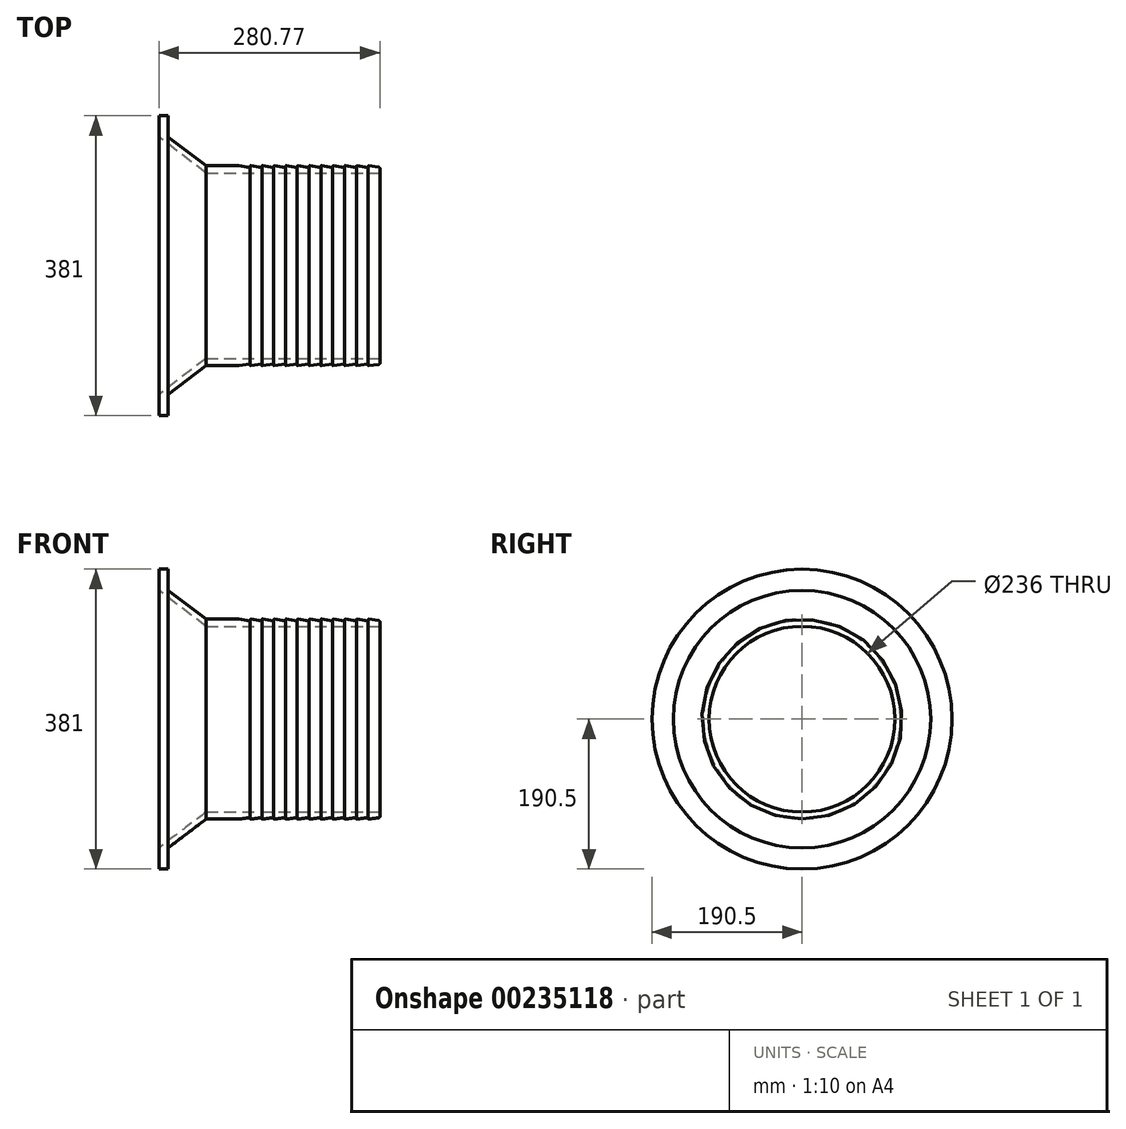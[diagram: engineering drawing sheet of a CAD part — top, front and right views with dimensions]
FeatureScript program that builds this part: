
annotation { "Feature Type Name" : "Feature", "Feature Type Description" : "" }
export const myFeature = defineFeature(function(context is Context, id is Id, definition is map)
    precondition{}
    {
        {
            var Q0;
            Q0=qCreatedBy(makeId("Front.planeOp"),FACE);
            var sketch = newSketch(context, id + "F0", { "sketchPlane" : qUnion([Q0])});
            skLineSegment(sketch, "E0", {"start": v(-1.73, 125.24) * mm, "end": v(-14.43, 127) * mm});
            skLineSegment(sketch, "E1", {"start": v(-15, 126.5) * mm, "end": v(-15, 125) * mm});
            skPoint(sketch, "E2.visualSharp", {"position": v(-15, 127.07) * mm});
            skArc(sketch, "E2.filletArc", {"start": v(-14.43, 127) * mm, "mid": v(-14.83, 126.88) * mm, "end": v(-15, 126.5) * mm});
            skLineSegment(sketch, "E3", {"start": v(0, 125) * mm, "end": v(-18.24, 125) * mm, "construction": true});
            skLineSegment(sketch, "E4", {"start": v(-7.53, 127) * mm, "end": v(-18.06, 127) * mm, "construction": true});
            skPoint(sketch, "E5", {"position": v(-14.5, 127) * mm});
            skLineSegment(sketch, "E6.1.0.0", {"start": v(-30, 126.5) * mm, "end": v(-30, 125) * mm});
            skArc(sketch, "E6.1.0.1", {"start": v(-29.43, 127) * mm, "mid": v(-29.83, 126.88) * mm, "end": v(-30, 126.5) * mm});
            skLineSegment(sketch, "E6.1.0.2", {"start": v(-15, 125) * mm, "end": v(-29.43, 127) * mm});
            skLineSegment(sketch, "E6.2.0.0", {"start": v(-45, 126.5) * mm, "end": v(-45, 125) * mm});
            skArc(sketch, "E6.2.0.1", {"start": v(-44.43, 127) * mm, "mid": v(-44.83, 126.88) * mm, "end": v(-45, 126.5) * mm});
            skLineSegment(sketch, "E6.2.0.2", {"start": v(-30, 125) * mm, "end": v(-44.43, 127) * mm});
            skLineSegment(sketch, "E6.3.0.0", {"start": v(-60, 126.5) * mm, "end": v(-60, 125) * mm});
            skArc(sketch, "E6.3.0.1", {"start": v(-59.43, 127) * mm, "mid": v(-59.83, 126.88) * mm, "end": v(-60, 126.5) * mm});
            skLineSegment(sketch, "E6.3.0.2", {"start": v(-45, 125) * mm, "end": v(-59.43, 127) * mm});
            skLineSegment(sketch, "E6.4.0.0", {"start": v(-75, 126.5) * mm, "end": v(-75, 125) * mm});
            skArc(sketch, "E6.4.0.1", {"start": v(-74.43, 127) * mm, "mid": v(-74.83, 126.88) * mm, "end": v(-75, 126.5) * mm});
            skLineSegment(sketch, "E6.4.0.2", {"start": v(-60, 125) * mm, "end": v(-74.43, 127) * mm});
            skLineSegment(sketch, "E6.5.0.0", {"start": v(-90, 126.5) * mm, "end": v(-90, 125) * mm});
            skArc(sketch, "E6.5.0.1", {"start": v(-89.43, 127) * mm, "mid": v(-89.83, 126.88) * mm, "end": v(-90, 126.5) * mm});
            skLineSegment(sketch, "E6.5.0.2", {"start": v(-75, 125) * mm, "end": v(-89.43, 127) * mm});
            skLineSegment(sketch, "E6.6.0.0", {"start": v(-105, 126.5) * mm, "end": v(-105, 125) * mm});
            skArc(sketch, "E6.6.0.1", {"start": v(-104.43, 127) * mm, "mid": v(-104.83, 126.88) * mm, "end": v(-105, 126.5) * mm});
            skLineSegment(sketch, "E6.6.0.2", {"start": v(-90, 125) * mm, "end": v(-104.43, 127) * mm});
            skLineSegment(sketch, "E6.7.0.0", {"start": v(-120, 126.5) * mm, "end": v(-120, 125) * mm});
            skArc(sketch, "E6.7.0.1", {"start": v(-119.43, 127) * mm, "mid": v(-119.83, 126.88) * mm, "end": v(-120, 126.5) * mm});
            skLineSegment(sketch, "E6.7.0.2", {"start": v(-105, 125) * mm, "end": v(-119.43, 127) * mm});
            skLineSegment(sketch, "E6.8.0.0", {"start": v(-135, 126.5) * mm, "end": v(-135, 125) * mm});
            skArc(sketch, "E6.8.0.1", {"start": v(-134.43, 127) * mm, "mid": v(-134.83, 126.88) * mm, "end": v(-135, 126.5) * mm});
            skLineSegment(sketch, "E6.8.0.2", {"start": v(-120, 125) * mm, "end": v(-134.43, 127) * mm});
            skLineSegment(sketch, "E6.9.0.0", {"start": v(-150, 126.5) * mm, "end": v(-150, 125) * mm});
            skArc(sketch, "E6.9.0.1", {"start": v(-149.43, 127) * mm, "mid": v(-149.83, 126.88) * mm, "end": v(-150, 126.5) * mm});
            skLineSegment(sketch, "E6.9.0.2", {"start": v(-135, 125) * mm, "end": v(-149.43, 127) * mm});
            skLineSegment(sketch, "E6.10.0.0", {"start": v(-165, 126.5) * mm, "end": v(-165, 125) * mm});
            skArc(sketch, "E6.10.0.1", {"start": v(-164.43, 127) * mm, "mid": v(-164.83, 126.88) * mm, "end": v(-165, 126.5) * mm});
            skLineSegment(sketch, "E6.10.0.2", {"start": v(-150, 125) * mm, "end": v(-164.43, 127) * mm});
            skLineSegment(sketch, "E6.11.0.0", {"start": v(-180, 126.5) * mm, "end": v(-180, 125) * mm});
            skArc(sketch, "E6.11.0.1", {"start": v(-179.43, 127) * mm, "mid": v(-179.83, 126.88) * mm, "end": v(-180, 126.5) * mm});
            skLineSegment(sketch, "E6.11.0.2", {"start": v(-165, 125) * mm, "end": v(-179.43, 127) * mm});
            skLineSegment(sketch, "E6.direction1", {"start": v(-15, 125) * mm, "end": v(-30, 125) * mm, "construction": true});
            skLineSegment(sketch, "E7", {"start": v(-179.5, 127) * mm, "end": v(-220.77, 127) * mm});
            skLineSegment(sketch, "E8", {"start": v(0, 123.26) * mm, "end": v(0, 120) * mm});
            skLineSegment(sketch, "E9", {"start": v(-2, 118) * mm, "end": v(-220.77, 118) * mm});
            skPoint(sketch, "E10.visualSharp", {"position": v(0, 125) * mm});
            skArc(sketch, "E10.filletArc", {"start": v(0, 123.26) * mm, "mid": v(-0.5, 124.57) * mm, "end": v(-1.73, 125.24) * mm});
            skPoint(sketch, "E11.visualSharp", {"position": v(0, 118) * mm});
            skArc(sketch, "E11.filletArc", {"start": v(-2, 118) * mm, "mid": v(-0.59, 118.59) * mm, "end": v(0, 120) * mm});
            skLineSegment(sketch, "E12", {"start": v(-220.77, 127) * mm, "end": v(-268.9, 163.5) * mm});
            skLineSegment(sketch, "E13", {"start": v(-268.9, 163.5) * mm, "end": v(-268.9, 190.5) * mm});
            skLineSegment(sketch, "E14", {"start": v(-268.9, 190.5) * mm, "end": v(-280.77, 190.5) * mm});
            skLineSegment(sketch, "E15", {"start": v(-280.77, 190.5) * mm, "end": v(-280.77, 163.5) * mm});
            skLineSegment(sketch, "E16", {"start": v(-280.77, 163.5) * mm, "end": v(-220.77, 118) * mm});
            skLineSegment(sketch, "E17", {"start": v(0, 0) * mm, "end": v(-315.6, 0) * mm, "construction": true});
            skLineSegment(sketch, "E18", {"start": v(-220.77, 127) * mm, "end": v(-220.77, 83.2) * mm, "construction": true});
            skSolve(sketch);
        }
        {
            var Q0;
            Q0=qCreatedBy(makeId("Front.planeOp"),FACE);
            var sketch = newSketch(context, id + "F1", { "sketchPlane" : qUnion([Q0])});
            skLineSegment(sketch, "E19", {"start": v(45.17, 0) * mm, "end": v(-335.63, 0) * mm, "construction": true});
            skSolve(sketch);
        }
        {
            var Q0;
            Q0=makeQuery(id+"F0.imprint","IMPRINT",FACE,{"disambiguationData":[TD([[makeQuery(id+"F0.imprint","IMPRINT",EDGE,{"derivedFrom":sQuery(id+"F0.wireOp",EDGE,"E0")}),1.0]])]});
            var Q1;
            Q1=sQuery(id+"F1.wireOp",EDGE,"E19");
            revolve(context, id + "F2", {"entities" : qUnion([Q0]), "axis" : qUnion([Q1]), "revolveType" : RevolveType.FULL});
        }
    });
